# Revit family: WBC_W_F_2vakken Hor_1vak Ver
name_source: partatom
category: Windows
revit_build: Autodesk Revit Architecture 2013 (Build: 20120221_2030(x64)
units: mm (PartAtom-declared; Revit-internal decimal feet)

## types (23) — shared parameters
Aanzicht Kader 110mm = No
Aanzicht Kader 68mm = Yes
Aanzicht Kader 78mm = No
Aanzicht Kader 88mm = No
Aanzicht Tussen Regel 110mm = No
Aanzicht Tussen Regel 150mm = No
Aanzicht Tussen Regel 200mm = No
Aanzicht Tussen Regel 68mm = No
Aanzicht Tussen Regel 78mm = Yes
Aanzicht Tussen Regel 88mm = No
Aanzicht Tussen Stijl 110mm = No
Aanzicht Tussen Stijl 150mm = No
Aanzicht Tussen Stijl 200mm = No
Aanzicht Tussen Stijl 68mm = No
Aanzicht Tussen Stijl 78mm = Yes
Aanzicht Tussen Stijl 88mm = No
Aanzicht Vleugel 66mm = No
Aanzichtbreedte Kozijn Profielen_68_78_88_110_150mm = 68
Aanzichtbreedte Tussen Regels _68_78_88_110_150_200mm = 78
Aanzichtbreedte Tussen Stijlen _68_78_88_110_150_200mm = 78
Analytic Construction = <None>
Assembly Code = B2020110
Beslag Nen 5096 R.c. 3 = No
Beslag VerborgenScharnieren = No
Brandwerendheid_old = No
BreedteMaat_1 = 900 mm  [stored 2.95276 ft]
Diepte Versterking Binnenzijde_30_55_75 = 75 mm  [stored 0.246063 ft]
Diepte Versterking Buitenzijde_30_50_85 = 30 mm  [stored 0.0984252 ft]
Dikte Stelkozijn = 27 mm  [stored 0.0885827 ft]
Dikte Stelkozijn onderzijde = 27 mm  [stored 0.0885827 ft]
DikteStelkozijnOnderzijde_SpelingPui_BuitenbladMWOnderzijde = 17 mm  [stored 0.0557743 ft]
DikteStelkozijn_SpelingPui_BuitenbladMW = 17 mm  [stored 0.0557743 ft]
E = No
E_old = No
G = No
G_old = No
Glasdikte (totaal) = 29 mm  [stored 0.0951444 ft]
GlassType = Glass, Clear Glazing, Low E
H_old = No
HalveSpouw = 90 mm  [stored 0.295276 ft]
Handgreep A_line = Yes
Handgreep SI_line = No
Height = 1800 mm  [stored 5.90551 ft]
I = Yes
I_old = Yes
J = Yes
J_old = Yes
Keynote = 30.34
Manufacturer = Kawneer Nederland
Operation = IfcWindow
RT 72 = No
ScheduleType |RF| = Windows 06-2016
Speling Pui_ buitenblad MW = 10 mm  [stored 0.0328084 ft]
Speling Pui_buitenblad MW Onderzijde = 10 mm  [stored 0.0328084 ft]
Spouwdiepte = 180 mm  [stored 0.590551 ft]
Type Comments = Vrij te parameteriseren Revit Model
URL = http://www.alcoa.com
Versterking Binnenzijde = Yes
Versterking Buitenzijde = No
Wall Closure = By host
Width = 1800 mm  [stored 5.90551 ft]
zero-valued in all types: BreedteMaat_2, BreedteMaat_3, BreedteMaat_4, BreedteMaat_5, Hoogte Tussen regel 1, Hoogte Tussen regel 2, Hoogte Tussen regel 3, Hoogte Tussen regel 4, Hoogte Tussen regel 5

## per-type parameters (varying)
- WBC_W_F_2vakken Hor_1vak Ver: A=Yes; A_old=Yes; Aanzicht Vleugel 35mm=No; Aanzicht Vleugel 45mm=Yes; AanzichtLijnDraai=Yes; Aanzichtbreedte Raamvleugel Profielen _35_45_66mm=45; AanzichtlLijnVal=No; B=No; B_old=No; Beslag Draai=Yes; Beslag Draai kiep=No; Beslag Kiep voor draai=No; Beslag Nen 5096 R.c. 2=No; Beslag Resume 03=Handgreep A-line (niet afsluitbaar) artikel 276 177; Beslag Resume 04=Conform technisch handboek blad LM 4200-D-E; Beslag Resume 05=Inbraakwerend draairaambeslag; Beslag Valraam=No; Brandwerend volgens:=Nen 6069 criteria Ew30 mits uitgevoerd conform:; Brandwerend volgens:2=Rapport 2010-Efectis-R0226[Rev.4] Brandbeoordeling EW 30; Brandwerendheid=Yes; C=No; C_old=No; D=No; D_old=No; Default Sill Height=800 mm; Description=Kawneer RT 62  volgens:; Description 2=Standaard systeemomschrijving RT 62 standaard vlak; F=No; F_old=No; H=Yes; HalveSpouw_OffsetVkKozijn_Stelkozijn=104 mm; Kleur Binnenzijde=Kawneer RAL 9001; Kleur Binnenzijde Vleugel=Kawneer RAL 9001; Kleur Buitenzijde=<By Category>; Kleur Buitenzijde Vleugel=<By Category>; Kleur H&S=Kawneer Anodiseer kleur RVS-look; Model=NL-SfB naam + ALCOA Model CAT; NL-SfB-Code=31.22.22; OffsetVkKozijnVkStelkozijn=14 mm  [stored 0.0459318 ft]; RT 52=No; RT 62=Yes
- RT 52 Draai: A=Yes; A_old=Yes; Aanzicht Vleugel 35mm=Yes; Aanzicht Vleugel 45mm=No; AanzichtLijnDraai=Yes; Aanzichtbreedte Raamvleugel Profielen _35_45_66mm=35; AanzichtlLijnVal=No; B=No; B_old=No; Beslag Draai=Yes; Beslag Draai kiep=No; Beslag Kiep voor draai=No; Beslag Nen 5096 R.c. 2=No; Beslag Resume 03=Handgreep A-line (niet afsluitbaar) artikel 276 177; Beslag Resume 04=Conform technisch handboek blad LM 4200-D; Beslag Resume 05=Draairaambeslag; Beslag Valraam=No; Brandwerend volgens:=-; Brandwerend volgens:2=Niet van toepassing_geselecteerd; Brandwerendheid=No; C=No; C_old=No; D=No; D_old=No; Default Sill Height=1000 mm  [stored 3.28084 ft]; Description=Kawneer RT 52 volgens:; Description 2=Standaard systeemomschrijving RT 52 standaard vlak; F=No; F_old=No; H=No; HalveSpouw_OffsetVkKozijn_Stelkozijn=103 mm; Kleur Binnenzijde=<By Category>; Kleur Binnenzijde Vleugel=<By Category>; Kleur Buitenzijde=<By Category>; Kleur Buitenzijde Vleugel=<By Category>; Kleur H&S=<By Category>; Model=NL-SfB naam + ALCOA Model CAT; NL-SfB-Code=31.22.22; OffsetVkKozijnVkStelkozijn=13 mm; RT 52=Yes; RT 62=No
- RT 52 Draai Inbraakwerend: A=Yes; A_old=Yes; Aanzicht Vleugel 35mm=Yes; Aanzicht Vleugel 45mm=No; AanzichtLijnDraai=Yes; Aanzichtbreedte Raamvleugel Profielen _35_45_66mm=35; AanzichtlLijnVal=No; B=No; B_old=No; Beslag Draai=Yes; Beslag Draai kiep=No; Beslag Kiep voor draai=No; Beslag Nen 5096 R.c. 2=Yes; Beslag Resume 03=Handgreep A-line (afsluitbaar) artikel 276 178; Beslag Resume 04=Conform technisch handboek blad LM 4200-D-E; Beslag Resume 05=Inbraakwerend draairaambeslag; Beslag Valraam=No; Brandwerend volgens:=-; Brandwerend volgens:2=Niet van toepassing_geselecteerd; Brandwerendheid=No; C=No; C_old=No; D=Yes; D_old=Yes; Default Sill Height=1000 mm  [stored 3.28084 ft]; Description=Kawneer RT 52 volgens:; Description 2=Standaard systeemomschrijving RT 52 standaard vlak; F=No; F_old=No; H=No; HalveSpouw_OffsetVkKozijn_Stelkozijn=103 mm; Kleur Binnenzijde=<By Category>; Kleur Binnenzijde Vleugel=<By Category>; Kleur Buitenzijde=<By Category>; Kleur Buitenzijde Vleugel=<By Category>; Kleur H&S=<By Category>; Model=NL-SfB naam + ALCOA Model CAT; NL-SfB-Code=31.22.22; OffsetVkKozijnVkStelkozijn=13 mm; RT 52=Yes; RT 62=No
- RT 52 Draai Brandwerend: A=Yes; A_old=Yes; Aanzicht Vleugel 35mm=Yes; Aanzicht Vleugel 45mm=No; AanzichtLijnDraai=Yes; Aanzichtbreedte Raamvleugel Profielen _35_45_66mm=35; AanzichtlLijnVal=No; B=No; B_old=No; Beslag Draai=Yes; Beslag Draai kiep=No; Beslag Kiep voor draai=No; Beslag Nen 5096 R.c. 2=No; Beslag Resume 03=Handgreep A-line (niet afsluitbaar) artikel 276 177; Beslag Resume 04=Conform technisch handboek blad LM 4200-D-E; Beslag Resume 05=Inbraakwerend draairaambeslag; Beslag Valraam=No; Brandwerend volgens:=Niet mogelijk binnen dit systeem_kiest u RT 62 of RT 72; Brandwerend volgens:2=-; Brandwerendheid=Yes; C=No; C_old=No; D=No; D_old=No; Default Sill Height=1000 mm  [stored 3.28084 ft]; Description=Kawneer RT 52 volgens:; Description 2=Standaard systeemomschrijving RT 52 standaard vlak; F=No; F_old=No; H=Yes; HalveSpouw_OffsetVkKozijn_Stelkozijn=103 mm; Kleur Binnenzijde=<By Category>; Kleur Binnenzijde Vleugel=<By Category>; Kleur Buitenzijde=<By Category>; Kleur Buitenzijde Vleugel=<By Category>; Kleur H&S=<By Category>; Model=NL-SfB naam + ALCOA Model CAT; NL-SfB-Code=31.22.22; OffsetVkKozijnVkStelkozijn=13 mm; RT 52=Yes; RT 62=No
- RT 52 Draai kiep element: A=No; A_old=No; Aanzicht Vleugel 35mm=Yes; Aanzicht Vleugel 45mm=No; AanzichtLijnDraai=Yes; Aanzichtbreedte Raamvleugel Profielen _35_45_66mm=35; AanzichtlLijnVal=Yes; B=Yes; B_old=Yes; Beslag Draai=No; Beslag Draai kiep=Yes; Beslag Kiep voor draai=No; Beslag Nen 5096 R.c. 2=No; Beslag Resume 03=Handgreep A-line (niet afsluitbaar) artikel 276 177; Beslag Resume 04=Conform technisch handboek blad LM 4200-DK; Beslag Resume 05=Draai-kiep beslag; Beslag Valraam=No; Brandwerend volgens:=-; Brandwerend volgens:2=Niet van toepassing_geselecteerd; Brandwerendheid=No; C=No; C_old=No; D=No; D_old=No; Default Sill Height=1000 mm  [stored 3.28084 ft]; Description=Kawneer RT 52 volgens:; Description 2=Standaard systeemomschrijving RT 52 standaard vlak; F=No; F_old=No; H=No; HalveSpouw_OffsetVkKozijn_Stelkozijn=103 mm; Kleur Binnenzijde=<By Category>; Kleur Binnenzijde Vleugel=<By Category>; Kleur Buitenzijde=<By Category>; Kleur Buitenzijde Vleugel=<By Category>; Kleur H&S=<By Category>; Model=NL-SfB naam + ALCOA Model CAT; NL-SfB-Code=31.25.22; OffsetVkKozijnVkStelkozijn=13 mm; RT 52=Yes; RT 62=No
- RT 52 Draai kiep element Inbraakwerend: A=No; A_old=No; Aanzicht Vleugel 35mm=Yes; Aanzicht Vleugel 45mm=No; AanzichtLijnDraai=Yes; Aanzichtbreedte Raamvleugel Profielen _35_45_66mm=35; AanzichtlLijnVal=Yes; B=Yes; B_old=Yes; Beslag Draai=No; Beslag Draai kiep=Yes; Beslag Kiep voor draai=No; Beslag Nen 5096 R.c. 2=Yes; Beslag Resume 03=Handgreep A-line (afsluitbaar) artikel 276 178; Beslag Resume 04=Conform technisch handboek blad LM 4200- DK-E; Beslag Resume 05=Inbraakwerend draai-kiep beslag; Beslag Valraam=No; Brandwerend volgens:=-; Brandwerend volgens:2=Niet van toepassing_geselecteerd; Brandwerendheid=No; C=No; C_old=No; D=Yes; D_old=Yes; Default Sill Height=1000 mm  [stored 3.28084 ft]; Description=Kawneer RT 52 volgens:; Description 2=Standaard systeemomschrijving RT 52 standaard vlak; F=No; F_old=No; H=No; HalveSpouw_OffsetVkKozijn_Stelkozijn=103 mm; Kleur Binnenzijde=<By Category>; Kleur Binnenzijde Vleugel=<By Category>; Kleur Buitenzijde=<By Category>; Kleur Buitenzijde Vleugel=<By Category>; Kleur H&S=<By Category>; Model=NL-SfB naam + ALCOA Model CAT; NL-SfB-Code=31.25.22; OffsetVkKozijnVkStelkozijn=13 mm; RT 52=Yes; RT 62=No
- RT 52 Draai keip element Brandwerend: A=No; A_old=No; Aanzicht Vleugel 35mm=Yes; Aanzicht Vleugel 45mm=No; AanzichtLijnDraai=Yes; Aanzichtbreedte Raamvleugel Profielen _35_45_66mm=35; AanzichtlLijnVal=Yes; B=Yes; B_old=Yes; Beslag Draai=No; Beslag Draai kiep=Yes; Beslag Kiep voor draai=No; Beslag Nen 5096 R.c. 2=No; Beslag Resume 03=Handgreep A-line (niet afsluitbaar) artikel 276 177; Beslag Resume 04=Conform technisch handboek blad LM 4200- DK-E; Beslag Resume 05=Inbraakwerend draai-kiep beslag; Beslag Valraam=No; Brandwerend volgens:=Niet mogelijk binnen dit systeem_kiest u RT 62 of RT 72; Brandwerend volgens:2=-; Brandwerendheid=Yes; C=No; C_old=No; D=No; D_old=No; Default Sill Height=1000 mm  [stored 3.28084 ft]; Description=Kawneer RT 52 volgens:; Description 2=Standaard systeemomschrijving RT 52 standaard vlak; F=No; F_old=No; H=Yes; HalveSpouw_OffsetVkKozijn_Stelkozijn=103 mm; Kleur Binnenzijde=<By Category>; Kleur Binnenzijde Vleugel=<By Category>; Kleur Buitenzijde=<By Category>; Kleur Buitenzijde Vleugel=<By Category>; Kleur H&S=<By Category>; Model=NL-SfB naam + ALCOA Model CAT; NL-SfB-Code=31.25.22; OffsetVkKozijnVkStelkozijn=13 mm; RT 52=Yes; RT 62=No
- RT 52 Val raam element: A=No; A_old=No; Aanzicht Vleugel 35mm=Yes; Aanzicht Vleugel 45mm=No; AanzichtLijnDraai=No; Aanzichtbreedte Raamvleugel Profielen _35_45_66mm=35; AanzichtlLijnVal=Yes; B=No; B_old=No; Beslag Draai=No; Beslag Draai kiep=No; Beslag Kiep voor draai=No; Beslag Nen 5096 R.c. 2=No; Beslag Resume 03=Handgreep A-line (niet afsluitbaar) artikel 276 177; Beslag Resume 04=Conform technisch handboek blad LM 4200 -K/ZV; Beslag Resume 05=Valraambeslag; Beslag Valraam=Yes; Brandwerend volgens:=-; Brandwerend volgens:2=Niet van toepassing_geselecteerd; Brandwerendheid=No; C=No; C_old=No; D=No; D_old=No; Default Sill Height=1000 mm  [stored 3.28084 ft]; Description=Kawneer RT 52 volgens:; Description 2=Standaard systeemomschrijving RT 52 standaard vlak; F=Yes; F_old=Yes; H=No; HalveSpouw_OffsetVkKozijn_Stelkozijn=103 mm; Kleur Binnenzijde=<By Category>; Kleur Binnenzijde Vleugel=<By Category>; Kleur Buitenzijde=<By Category>; Kleur Buitenzijde Vleugel=<By Category>; Kleur H&S=<By Category>; Model=NL-SfB naam + ALCOA Model CAT; NL-SfB-Code=31.22.42; OffsetVkKozijnVkStelkozijn=13 mm; RT 52=Yes; RT 62=No
- RT 52 Val raam element Inbraakwerend: A=No; A_old=No; Aanzicht Vleugel 35mm=Yes; Aanzicht Vleugel 45mm=No; AanzichtLijnDraai=No; Aanzichtbreedte Raamvleugel Profielen _35_45_66mm=35; AanzichtlLijnVal=Yes; B=No; B_old=No; Beslag Draai=No; Beslag Draai kiep=No; Beslag Kiep voor draai=No; Beslag Nen 5096 R.c. 2=Yes; Beslag Resume 03=Handgreep A-line (afsluitbaar) artikel 276 178; Beslag Resume 04=Conform technisch handboek blad LM 4200-K/ZV-E; Beslag Resume 05=Inbraakwerend valraambeslag; Beslag Valraam=Yes; Brandwerend volgens:=-; Brandwerend volgens:2=Niet van toepassing_geselecteerd; Brandwerendheid=No; C=No; C_old=No; D=Yes; D_old=Yes; Default Sill Height=1000 mm  [stored 3.28084 ft]; Description=Kawneer RT 52 volgens:; Description 2=Standaard systeemomschrijving RT 52 standaard vlak; F=Yes; F_old=Yes; H=No; HalveSpouw_OffsetVkKozijn_Stelkozijn=103 mm; Kleur Binnenzijde=<By Category>; Kleur Binnenzijde Vleugel=<By Category>; Kleur Buitenzijde=<By Category>; Kleur Buitenzijde Vleugel=<By Category>; Kleur H&S=<By Category>; Model=NL-SfB naam + ALCOA Model CAT; NL-SfB-Code=31.22.42; OffsetVkKozijnVkStelkozijn=13 mm; RT 52=Yes; RT 62=No
- RT 52 Val raam element Brandwerend: A=No; A_old=No; Aanzicht Vleugel 35mm=Yes; Aanzicht Vleugel 45mm=No; AanzichtLijnDraai=No; Aanzichtbreedte Raamvleugel Profielen _35_45_66mm=35; AanzichtlLijnVal=Yes; B=No; B_old=No; Beslag Draai=No; Beslag Draai kiep=No; Beslag Kiep voor draai=No; Beslag Nen 5096 R.c. 2=Yes; Beslag Resume 03=Handgreep A-line (afsluitbaar) artikel 276 178; Beslag Resume 04=Conform technisch handboek blad LM 4200-K/ZV-E; Beslag Resume 05=Inbraakwerend valraambeslag; Beslag Valraam=Yes; Brandwerend volgens:=Niet mogelijk binnen dit systeem_kiest u RT 62 of RT 72; Brandwerend volgens:2=-; Brandwerendheid=Yes; C=No; C_old=No; D=Yes; D_old=Yes; Default Sill Height=1000 mm  [stored 3.28084 ft]; Description=Kawneer RT 52 volgens:; Description 2=Standaard systeemomschrijving RT 52 standaard vlak; F=Yes; F_old=Yes; H=Yes; HalveSpouw_OffsetVkKozijn_Stelkozijn=103 mm; Kleur Binnenzijde=<By Category>; Kleur Binnenzijde Vleugel=<By Category>; Kleur Buitenzijde=<By Category>; Kleur Buitenzijde Vleugel=<By Category>; Kleur H&S=<By Category>; Model=NL-SfB naam + ALCOA Model CAT; NL-SfB-Code=31.22.42; OffsetVkKozijnVkStelkozijn=13 mm; RT 52=Yes; RT 62=No
- RT 52 Kiep voor draai element: A=No; A_old=No; Aanzicht Vleugel 35mm=Yes; Aanzicht Vleugel 45mm=No; AanzichtLijnDraai=Yes; Aanzichtbreedte Raamvleugel Profielen _35_45_66mm=35; AanzichtlLijnVal=Yes; B=No; B_old=No; Beslag Draai=No; Beslag Draai kiep=No; Beslag Kiep voor draai=Yes; Beslag Nen 5096 R.c. 2=No; Beslag Resume 03=Handgreep A-line (niet afsluitbaar) artikel 276 177; Beslag Resume 04=Conform technisch handboek blad LM 4200-TBT; Beslag Resume 05=Kiep-voor-draai beslag; Beslag Valraam=No; Brandwerend volgens:=-; Brandwerend volgens:2=Niet van toepassing_geselecteerd; Brandwerendheid=No; C=Yes; C_old=Yes; D=No; D_old=No; Default Sill Height=1000 mm  [stored 3.28084 ft]; Description=Kawneer RT 52 volgens:; Description 2=Standaard systeemomschrijving RT 52 standaard vlak; F=No; F_old=No; H=No; HalveSpouw_OffsetVkKozijn_Stelkozijn=103 mm; Kleur Binnenzijde=<By Category>; Kleur Binnenzijde Vleugel=<By Category>; Kleur Buitenzijde=<By Category>; Kleur Buitenzijde Vleugel=<By Category>; Kleur H&S=<By Category>; Model=NL-SfB naam + ALCOA Model CAT; NL-SfB-Code=31.25.22; OffsetVkKozijnVkStelkozijn=13 mm; RT 52=Yes; RT 62=No
- RT 52 Kiep voor draai elemnent Inbraakwerend: A=No; A_old=No; Aanzicht Vleugel 35mm=Yes; Aanzicht Vleugel 45mm=No; AanzichtLijnDraai=Yes; Aanzichtbreedte Raamvleugel Profielen _35_45_66mm=35; AanzichtlLijnVal=Yes; B=No; B_old=No; Beslag Draai=No; Beslag Draai kiep=No; Beslag Kiep voor draai=Yes; Beslag Nen 5096 R.c. 2=Yes; Beslag Resume 03=Handgreep A-line (afsluitbaar) artikel 276 178; Beslag Resume 04=Conform technisch handboek blad LM 4200-TBT-E; Beslag Resume 05=Kiep-voor-draai beslag; Beslag Valraam=No; Brandwerend volgens:=-; Brandwerend volgens:2=Niet van toepassing_geselecteerd; Brandwerendheid=No; C=Yes; C_old=Yes; D=Yes; D_old=Yes; Default Sill Height=1000 mm  [stored 3.28084 ft]; Description=Kawneer RT 52 volgens:; Description 2=Standaard systeemomschrijving RT 52 standaard vlak; F=No; F_old=No; H=No; HalveSpouw_OffsetVkKozijn_Stelkozijn=103 mm; Kleur Binnenzijde=<By Category>; Kleur Binnenzijde Vleugel=<By Category>; Kleur Buitenzijde=<By Category>; Kleur Buitenzijde Vleugel=<By Category>; Kleur H&S=<By Category>; Model=NL-SfB naam + ALCOA Model CAT; NL-SfB-Code=31.25.22; OffsetVkKozijnVkStelkozijn=13 mm; RT 52=Yes; RT 62=No
- RT 52 Kiep voor draai element Brandwerend: A=No; A_old=No; Aanzicht Vleugel 35mm=Yes; Aanzicht Vleugel 45mm=No; AanzichtLijnDraai=Yes; Aanzichtbreedte Raamvleugel Profielen _35_45_66mm=35; AanzichtlLijnVal=Yes; B=No; B_old=No; Beslag Draai=No; Beslag Draai kiep=No; Beslag Kiep voor draai=Yes; Beslag Nen 5096 R.c. 2=No; Beslag Resume 03=Handgreep A-line (niet afsluitbaar) artikel 276 177; Beslag Resume 04=Conform technisch handboek blad LM 4200-TBT-E; Beslag Resume 05=Kiep-voor-draai beslag; Beslag Valraam=No; Brandwerend volgens:=Niet mogelijk binnen dit systeem_kiest u RT 62 of RT 72; Brandwerend volgens:2=-; Brandwerendheid=Yes; C=Yes; C_old=Yes; D=No; D_old=No; Default Sill Height=1000 mm  [stored 3.28084 ft]; Description=Kawneer RT 52 volgens:; Description 2=Standaard systeemomschrijving RT 52 standaard vlak; F=No; F_old=No; H=Yes; HalveSpouw_OffsetVkKozijn_Stelkozijn=103 mm; Kleur Binnenzijde=<By Category>; Kleur Binnenzijde Vleugel=<By Category>; Kleur Buitenzijde=<By Category>; Kleur Buitenzijde Vleugel=<By Category>; Kleur H&S=<By Category>; Model=NL-SfB naam + ALCOA Model CAT; NL-SfB-Code=31.25.22; OffsetVkKozijnVkStelkozijn=13 mm; RT 52=Yes; RT 62=No
- RT 62 Draai kiep element: A=No; A_old=No; Aanzicht Vleugel 35mm=Yes; Aanzicht Vleugel 45mm=No; AanzichtLijnDraai=Yes; Aanzichtbreedte Raamvleugel Profielen _35_45_66mm=35; AanzichtlLijnVal=Yes; B=Yes; B_old=Yes; Beslag Draai=No; Beslag Draai kiep=Yes; Beslag Kiep voor draai=No; Beslag Nen 5096 R.c. 2=No; Beslag Resume 03=Handgreep A-line (niet afsluitbaar) artikel 276 177; Beslag Resume 04=Conform technisch handboek blad LM 4200-DK; Beslag Resume 05=Draai-kiep beslag; Beslag Valraam=No; Brandwerend volgens:=-; Brandwerend volgens:2=Niet van toepassing_geselecteerd; Brandwerendheid=No; C=No; C_old=No; D=No; D_old=No; Default Sill Height=1000 mm  [stored 3.28084 ft]; Description=Kawneer RT 62  volgens:; Description 2=Standaard systeemomschrijving RT 62 standaard vlak; F=No; F_old=No; H=No; HalveSpouw_OffsetVkKozijn_Stelkozijn=103 mm; Kleur Binnenzijde=<By Category>; Kleur Binnenzijde Vleugel=<By Category>; Kleur Buitenzijde=<By Category>; Kleur Buitenzijde Vleugel=<By Category>; Kleur H&S=<By Category>; Model=NL-SfB naam + ALCOA Model CAT; NL-SfB-Code=31.25.22; OffsetVkKozijnVkStelkozijn=13 mm; RT 52=No; RT 62=Yes
- RT 62 Draai kiep element Inbraakwerend: A=No; A_old=No; Aanzicht Vleugel 35mm=Yes; Aanzicht Vleugel 45mm=No; AanzichtLijnDraai=Yes; Aanzichtbreedte Raamvleugel Profielen _35_45_66mm=35; AanzichtlLijnVal=Yes; B=Yes; B_old=Yes; Beslag Draai=No; Beslag Draai kiep=Yes; Beslag Kiep voor draai=No; Beslag Nen 5096 R.c. 2=Yes; Beslag Resume 03=Handgreep A-line (afsluitbaar) artikel 276 178; Beslag Resume 04=Conform technisch handboek blad LM 4200- DK-E; Beslag Resume 05=Inbraakwerend draai-kiep beslag; Beslag Valraam=No; Brandwerend volgens:=-; Brandwerend volgens:2=Niet van toepassing_geselecteerd; Brandwerendheid=No; C=No; C_old=No; D=Yes; D_old=Yes; Default Sill Height=1000 mm  [stored 3.28084 ft]; Description=Kawneer RT 62  volgens:; Description 2=Standaard systeemomschrijving RT 62 standaard vlak; F=No; F_old=No; H=No; HalveSpouw_OffsetVkKozijn_Stelkozijn=103 mm; Kleur Binnenzijde=<By Category>; Kleur Binnenzijde Vleugel=<By Category>; Kleur Buitenzijde=<By Category>; Kleur Buitenzijde Vleugel=<By Category>; Kleur H&S=<By Category>; Model=NL-SfB naam + ALCOA Model CAT; NL-SfB-Code=31.25.22; OffsetVkKozijnVkStelkozijn=13 mm; RT 52=No; RT 62=Yes
- RT 62 Draai kiep element Brandwerend: A=No; A_old=No; Aanzicht Vleugel 35mm=Yes; Aanzicht Vleugel 45mm=No; AanzichtLijnDraai=Yes; Aanzichtbreedte Raamvleugel Profielen _35_45_66mm=35; AanzichtlLijnVal=Yes; B=Yes; B_old=Yes; Beslag Draai=No; Beslag Draai kiep=Yes; Beslag Kiep voor draai=No; Beslag Nen 5096 R.c. 2=No; Beslag Resume 03=Handgreep A-line (niet afsluitbaar) artikel 276 177; Beslag Resume 04=Conform technisch handboek blad LM 4200- DK-E; Beslag Resume 05=Inbraakwerend draai-kiep beslag; Beslag Valraam=No; Brandwerend volgens:=Nen 6069 criteria Ew30 mits uitgevoerd conform:; Brandwerend volgens:2=Rapport 2010-Efectis-R0226[Rev.4] Brandbeoordeling EW 30; Brandwerendheid=Yes; C=No; C_old=No; D=No; D_old=No; Default Sill Height=1000 mm  [stored 3.28084 ft]; Description=Kawneer RT 62  volgens:; Description 2=Standaard systeemomschrijving RT 62 standaard vlak; F=No; F_old=No; H=Yes; HalveSpouw_OffsetVkKozijn_Stelkozijn=103 mm; Kleur Binnenzijde=<By Category>; Kleur Binnenzijde Vleugel=<By Category>; Kleur Buitenzijde=<By Category>; Kleur Buitenzijde Vleugel=<By Category>; Kleur H&S=<By Category>; Model=NL-SfB naam + ALCOA Model CAT; NL-SfB-Code=31.25.22; OffsetVkKozijnVkStelkozijn=13 mm; RT 52=No; RT 62=Yes
- RT 62 Draai element: A=Yes; A_old=Yes; Aanzicht Vleugel 35mm=Yes; Aanzicht Vleugel 45mm=No; AanzichtLijnDraai=Yes; Aanzichtbreedte Raamvleugel Profielen _35_45_66mm=35; AanzichtlLijnVal=No; B=No; B_old=No; Beslag Draai=Yes; Beslag Draai kiep=No; Beslag Kiep voor draai=No; Beslag Nen 5096 R.c. 2=No; Beslag Resume 03=Handgreep A-line (niet afsluitbaar) artikel 276 177; Beslag Resume 04=Conform technisch handboek blad LM 4200-D-E; Beslag Resume 05=Inbraakwerend draairaambeslag; Beslag Valraam=No; Brandwerend volgens:=Nen 6069 criteria Ew30 mits uitgevoerd conform:; Brandwerend volgens:2=Rapport 2010-Efectis-R0226[Rev.4] Brandbeoordeling EW 30; Brandwerendheid=Yes; C=No; C_old=No; D=No; D_old=No; Default Sill Height=1000 mm  [stored 3.28084 ft]; Description=Kawneer RT 62  volgens:; Description 2=Standaard systeemomschrijving RT 62 standaard vlak; F=No; F_old=No; H=Yes; HalveSpouw_OffsetVkKozijn_Stelkozijn=103 mm; Kleur Binnenzijde=<By Category>; Kleur Binnenzijde Vleugel=<By Category>; Kleur Buitenzijde=<By Category>; Kleur Buitenzijde Vleugel=<By Category>; Kleur H&S=<By Category>; Model=NL-SfB naam + ALCOA Model CAT; NL-SfB-Code=31.22.22; OffsetVkKozijnVkStelkozijn=13 mm; RT 52=No; RT 62=Yes
- RT 62 Draai element inbraakwerend: A=Yes; A_old=Yes; Aanzicht Vleugel 35mm=Yes; Aanzicht Vleugel 45mm=No; AanzichtLijnDraai=Yes; Aanzichtbreedte Raamvleugel Profielen _35_45_66mm=35; AanzichtlLijnVal=No; B=No; B_old=No; Beslag Draai=Yes; Beslag Draai kiep=No; Beslag Kiep voor draai=No; Beslag Nen 5096 R.c. 2=Yes; Beslag Resume 03=Handgreep A-line (afsluitbaar) artikel 276 178; Beslag Resume 04=Conform technisch handboek blad LM 4200-D-E; Beslag Resume 05=Inbraakwerend draairaambeslag; Beslag Valraam=No; Brandwerend volgens:=-; Brandwerend volgens:2=Niet van toepassing_geselecteerd; Brandwerendheid=No; C=No; C_old=No; D=Yes; D_old=Yes; Default Sill Height=1000 mm  [stored 3.28084 ft]; Description=Kawneer RT 62  volgens:; Description 2=Standaard systeemomschrijving RT 62 standaard vlak; F=No; F_old=No; H=No; HalveSpouw_OffsetVkKozijn_Stelkozijn=103 mm; Kleur Binnenzijde=<By Category>; Kleur Binnenzijde Vleugel=<By Category>; Kleur Buitenzijde=<By Category>; Kleur Buitenzijde Vleugel=<By Category>; Kleur H&S=<By Category>; Model=NL-SfB naam + ALCOA Model CAT; NL-SfB-Code=31.22.22; OffsetVkKozijnVkStelkozijn=13 mm; RT 52=No; RT 62=Yes
- RT 62 Draai element brandwerend: A=Yes; A_old=Yes; Aanzicht Vleugel 35mm=Yes; Aanzicht Vleugel 45mm=No; AanzichtLijnDraai=Yes; Aanzichtbreedte Raamvleugel Profielen _35_45_66mm=35; AanzichtlLijnVal=No; B=No; B_old=No; Beslag Draai=Yes; Beslag Draai kiep=No; Beslag Kiep voor draai=No; Beslag Nen 5096 R.c. 2=No; Beslag Resume 03=Handgreep A-line (niet afsluitbaar) artikel 276 177; Beslag Resume 04=Conform technisch handboek blad LM 4200-D-E; Beslag Resume 05=Inbraakwerend draairaambeslag; Beslag Valraam=No; Brandwerend volgens:=Nen 6069 criteria Ew30 mits uitgevoerd conform:; Brandwerend volgens:2=Rapport 2010-Efectis-R0226[Rev.4] Brandbeoordeling EW 30; Brandwerendheid=Yes; C=No; C_old=No; D=No; D_old=No; Default Sill Height=1000 mm  [stored 3.28084 ft]; Description=Kawneer RT 62  volgens:; Description 2=Standaard systeemomschrijving RT 62 standaard vlak; F=No; F_old=No; H=Yes; HalveSpouw_OffsetVkKozijn_Stelkozijn=103 mm; Kleur Binnenzijde=<By Category>; Kleur Binnenzijde Vleugel=<By Category>; Kleur Buitenzijde=<By Category>; Kleur Buitenzijde Vleugel=<By Category>; Kleur H&S=<By Category>; Model=NL-SfB naam + ALCOA Model CAT; NL-SfB-Code=31.22.22; OffsetVkKozijnVkStelkozijn=13 mm; RT 52=No; RT 62=Yes
- RT 62 Val raam element: A=No; A_old=No; Aanzicht Vleugel 35mm=Yes; Aanzicht Vleugel 45mm=No; AanzichtLijnDraai=No; Aanzichtbreedte Raamvleugel Profielen _35_45_66mm=35; AanzichtlLijnVal=Yes; B=No; B_old=No; Beslag Draai=No; Beslag Draai kiep=No; Beslag Kiep voor draai=No; Beslag Nen 5096 R.c. 2=No; Beslag Resume 03=Handgreep A-line (niet afsluitbaar) artikel 276 177; Beslag Resume 04=Conform technisch handboek blad LM 4200 -K/ZV; Beslag Resume 05=Valraambeslag; Beslag Valraam=Yes; Brandwerend volgens:=-; Brandwerend volgens:2=Niet van toepassing_geselecteerd; Brandwerendheid=No; C=No; C_old=No; D=No; D_old=No; Default Sill Height=1000 mm  [stored 3.28084 ft]; Description=Kawneer RT 62  volgens:; Description 2=Standaard systeemomschrijving RT 62 standaard vlak; F=Yes; F_old=Yes; H=No; HalveSpouw_OffsetVkKozijn_Stelkozijn=103 mm; Kleur Binnenzijde=<By Category>; Kleur Binnenzijde Vleugel=<By Category>; Kleur Buitenzijde=<By Category>; Kleur Buitenzijde Vleugel=<By Category>; Kleur H&S=<By Category>; Model=NL-SfB naam + ALCOA Model CAT; NL-SfB-Code=31.22.42; OffsetVkKozijnVkStelkozijn=13 mm; RT 52=No; RT 62=Yes
- RT 62 Val raam element inbraakwerend: A=No; A_old=No; Aanzicht Vleugel 35mm=Yes; Aanzicht Vleugel 45mm=No; AanzichtLijnDraai=No; Aanzichtbreedte Raamvleugel Profielen _35_45_66mm=35; AanzichtlLijnVal=Yes; B=No; B_old=No; Beslag Draai=No; Beslag Draai kiep=No; Beslag Kiep voor draai=No; Beslag Nen 5096 R.c. 2=Yes; Beslag Resume 03=Handgreep A-line (afsluitbaar) artikel 276 178; Beslag Resume 04=Conform technisch handboek blad LM 4200-K/ZV-E; Beslag Resume 05=Inbraakwerend valraambeslag; Beslag Valraam=Yes; Brandwerend volgens:=-; Brandwerend volgens:2=Niet van toepassing_geselecteerd; Brandwerendheid=No; C=No; C_old=No; D=Yes; D_old=Yes; Default Sill Height=1000 mm  [stored 3.28084 ft]; Description=Kawneer RT 62  volgens:; Description 2=Standaard systeemomschrijving RT 62 standaard vlak; F=Yes; F_old=Yes; H=No; HalveSpouw_OffsetVkKozijn_Stelkozijn=103 mm; Kleur Binnenzijde=<By Category>; Kleur Binnenzijde Vleugel=<By Category>; Kleur Buitenzijde=<By Category>; Kleur Buitenzijde Vleugel=<By Category>; Kleur H&S=<By Category>; Model=NL-SfB naam + ALCOA Model CAT; NL-SfB-Code=31.22.42; OffsetVkKozijnVkStelkozijn=13 mm; RT 52=No; RT 62=Yes
- RT 62 Val raam element brandwerend: A=No; A_old=No; Aanzicht Vleugel 35mm=Yes; Aanzicht Vleugel 45mm=No; AanzichtLijnDraai=No; Aanzichtbreedte Raamvleugel Profielen _35_45_66mm=35; AanzichtlLijnVal=Yes; B=No; B_old=No; Beslag Draai=No; Beslag Draai kiep=No; Beslag Kiep voor draai=No; Beslag Nen 5096 R.c. 2=No; Beslag Resume 03=Handgreep A-line (niet afsluitbaar) artikel 276 177; Beslag Resume 04=Conform technisch handboek blad LM 4200-K/ZV-E; Beslag Resume 05=Inbraakwerend valraambeslag; Beslag Valraam=Yes; Brandwerend volgens:=Nen 6069 criteria Ew30 mits uitgevoerd conform:; Brandwerend volgens:2=Rapport 2010-Efectis-R0226[Rev.4] Brandbeoordeling EW 30; Brandwerendheid=Yes; C=No; C_old=No; D=No; D_old=No; Default Sill Height=1000 mm  [stored 3.28084 ft]; Description=Kawneer RT 62  volgens:; Description 2=Standaard systeemomschrijving RT 62 standaard vlak; F=Yes; F_old=Yes; H=Yes; HalveSpouw_OffsetVkKozijn_Stelkozijn=103 mm; Kleur Binnenzijde=<By Category>; Kleur Binnenzijde Vleugel=<By Category>; Kleur Buitenzijde=<By Category>; Kleur Buitenzijde Vleugel=<By Category>; Kleur H&S=<By Category>; Model=NL-SfB naam + ALCOA Model CAT; NL-SfB-Code=31.22.42; OffsetVkKozijnVkStelkozijn=13 mm; RT 52=No; RT 62=Yes
- RT 62 Kiep voor draai element: A=No; A_old=No; Aanzicht Vleugel 35mm=Yes; Aanzicht Vleugel 45mm=No; AanzichtLijnDraai=Yes; Aanzichtbreedte Raamvleugel Profielen _35_45_66mm=35; AanzichtlLijnVal=Yes; B=No; B_old=No; Beslag Draai=No; Beslag Draai kiep=No; Beslag Kiep voor draai=Yes; Beslag Nen 5096 R.c. 2=No; Beslag Resume 03=Handgreep A-line (niet afsluitbaar) artikel 276 177; Beslag Resume 04=Conform technisch handboek blad LM 4200-TBT; Beslag Resume 05=Kiep-voor-draai beslag; Beslag Valraam=No; Brandwerend volgens:=-; Brandwerend volgens:2=Niet van toepassing_geselecteerd; Brandwerendheid=No; C=Yes; C_old=Yes; D=No; D_old=No; Default Sill Height=1000 mm  [stored 3.28084 ft]; Description=Kawneer RT 62  volgens:; Description 2=Standaard systeemomschrijving RT 62 standaard vlak; F=No; F_old=No; H=No; HalveSpouw_OffsetVkKozijn_Stelkozijn=103 mm; Kleur Binnenzijde=Kawneer RAL 9010; Kleur Binnenzijde Vleugel=Kawneer RAL 9010; Kleur Buitenzijde=Kawneer RAL 9010; Kleur Buitenzijde Vleugel=Kawneer RAL 9010; Kleur H&S=Kawneer Anodiseer kleur RVS-look; Model=NL-SfB naam; NL-SfB-Code=31.25.22; OffsetVkKozijnVkStelkozijn=13 mm; RT 52=No; RT 62=Yes

note: [stored X ft] marks values corroborated as IEEE doubles in the binary element streams (Revit-internal decimal feet)

## geometry (parser evidence)
native form markers: Blend x22, Sweep x31
no freeform markers — native parametric forms only
